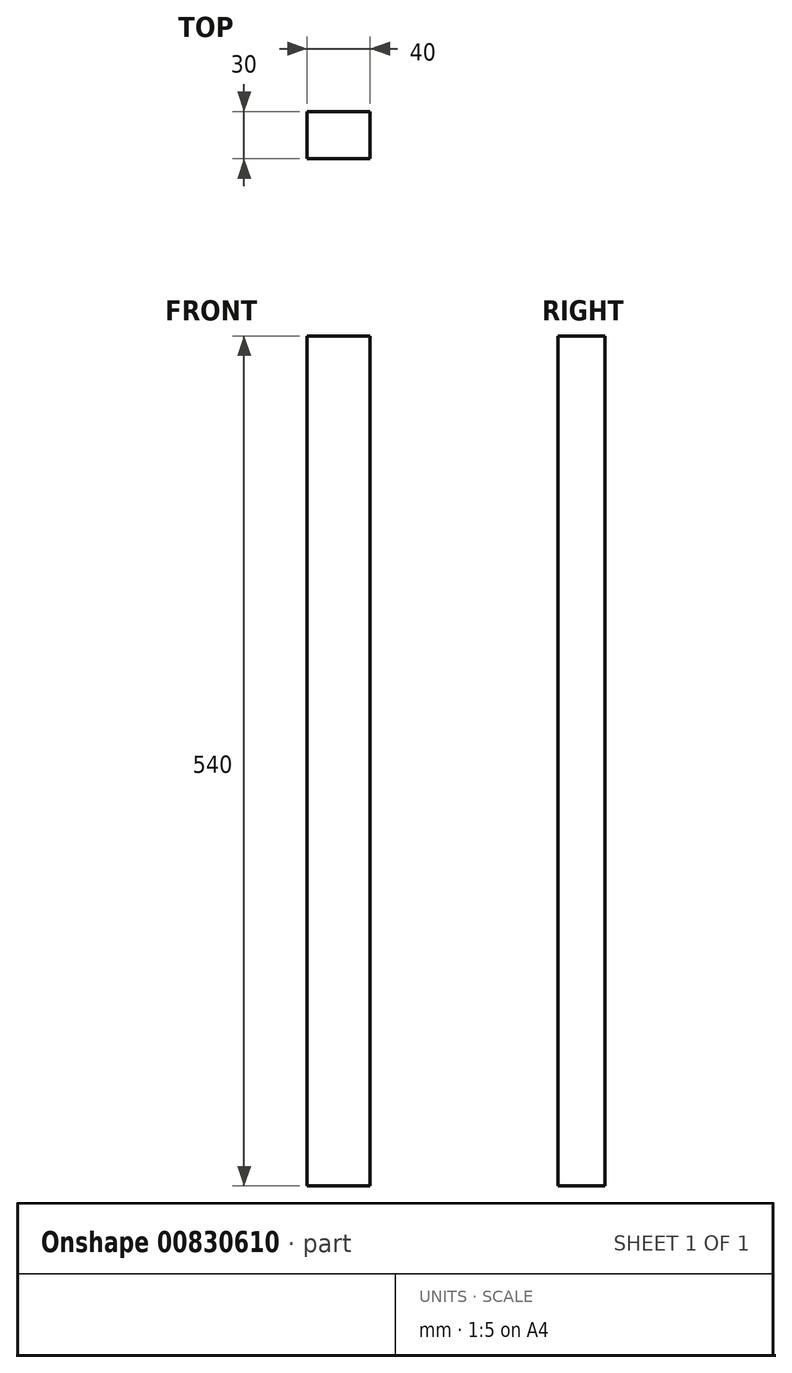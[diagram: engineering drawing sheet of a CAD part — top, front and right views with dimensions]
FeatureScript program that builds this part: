
annotation { "Feature Type Name" : "Feature", "Feature Type Description" : "" }
export const myFeature = defineFeature(function(context is Context, id is Id, definition is map)
    precondition{}
    {
        {
            var Q0;
            Q0=qCreatedBy(makeId("Top.planeOp"),FACE);
            var sketch = newSketch(context, id + "F0", { "sketchPlane" : qUnion([Q0])});
            skLineSegment(sketch, "E0.bottom", {"start": v(3.01, 0) * mm, "end": v(43.01, 0) * mm});
            skLineSegment(sketch, "E0.top", {"start": v(3.01, 30) * mm, "end": v(43.01, 30) * mm});
            skLineSegment(sketch, "E0.left", {"start": v(3.01, 0) * mm, "end": v(3.01, 30) * mm});
            skLineSegment(sketch, "E0.right", {"start": v(43.01, 0) * mm, "end": v(43.01, 30) * mm});
            skSolve(sketch);
        }
        {
            var Q0;
            Q0=makeQuery(id+"F0.imprint","IMPRINT",FACE,{"disambiguationData":[TD([[makeQuery(id+"F0.imprint","IMPRINT",EDGE,{"derivedFrom":sQuery(id+"F0.wireOp",EDGE,"E0.bottom")}),1.0]])]});
            extrude(context, id + "F1", {"entities" : qUnion([Q0]), "depth" : 540 * mm, "offsetDistance" : 25 * mm});
        }
    });
